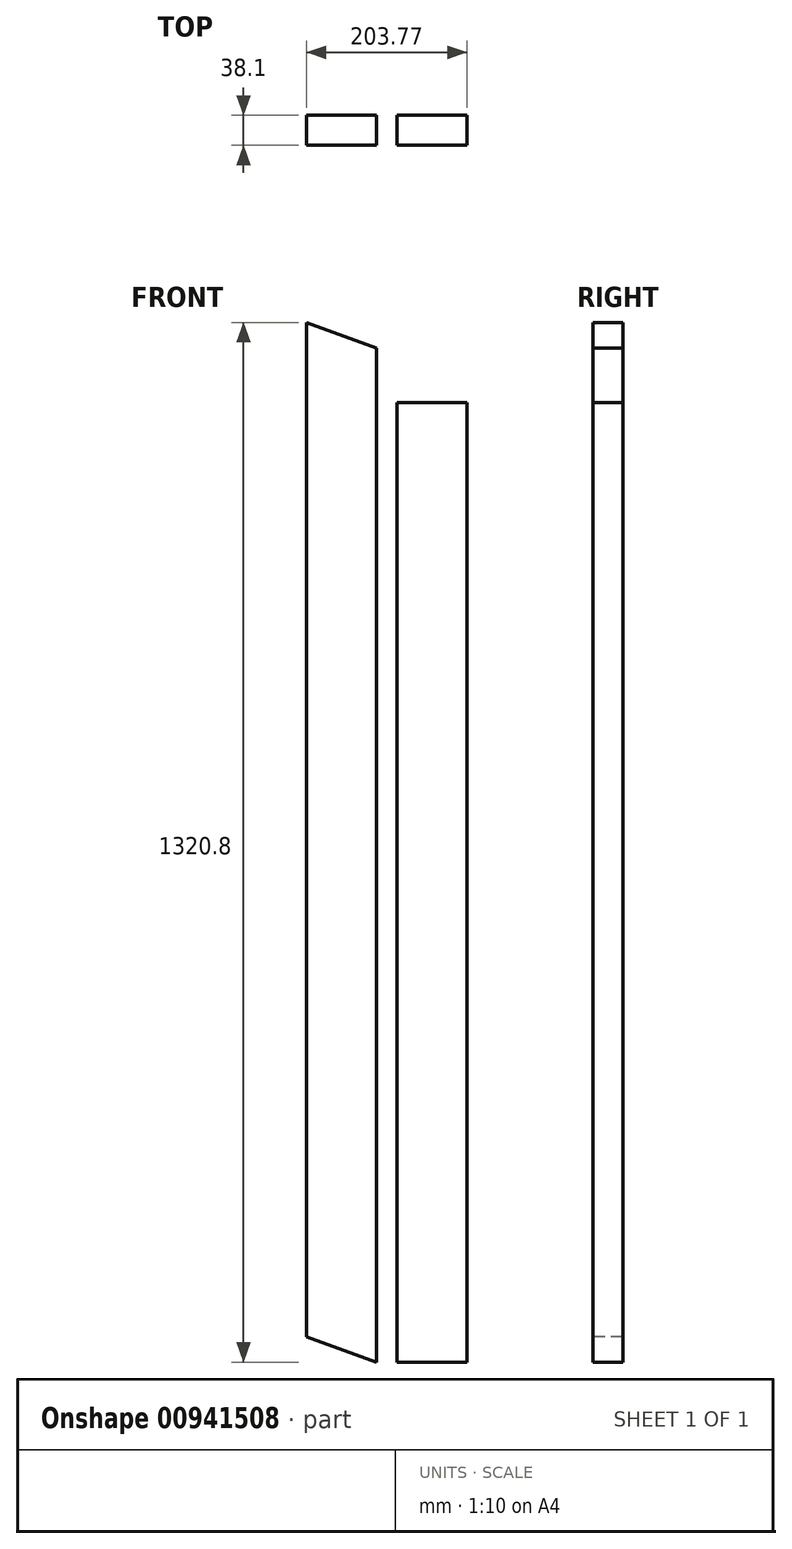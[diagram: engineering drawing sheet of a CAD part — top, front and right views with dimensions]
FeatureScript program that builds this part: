
annotation { "Feature Type Name" : "Feature", "Feature Type Description" : "" }
export const myFeature = defineFeature(function(context is Context, id is Id, definition is map)
    precondition{}
    {
        {
            var Q0;
            Q0=qCreatedBy(makeId("Front.planeOp"),FACE);
            var sketch = newSketch(context, id + "F0", { "sketchPlane" : qUnion([Q0])});
            skLineSegment(sketch, "E0.bottom", {"start": v(0, 0) * mm, "end": v(88.9, 0) * mm});
            skLineSegment(sketch, "E0.top", {"start": v(0, 1219.2) * mm, "end": v(88.9, 1219.2) * mm});
            skLineSegment(sketch, "E0.left", {"start": v(0, 0) * mm, "end": v(0, 1219.2) * mm});
            skLineSegment(sketch, "E0.right", {"start": v(88.9, 0) * mm, "end": v(88.9, 1219.2) * mm});
            skSolve(sketch);
        }
        {
            var Q0;
            Q0 = qSketchRegion(id + "F0", true);
            extrude(context, id + "F1", {"entities" : qUnion([Q0]), "depth" : 38.1 * mm, "offsetDistance" : 25.4 * mm});
        }
        {
            var Q0;
            Q0=qCreatedBy(makeId("Front.planeOp"),FACE);
            var sketch = newSketch(context, id + "F2", { "sketchPlane" : qUnion([Q0])});
            skLineSegment(sketch, "E1.bottom", {"start": v(-25.97, 0) * mm, "end": v(-114.87, 0) * mm});
            skLineSegment(sketch, "E1.top", {"start": v(-25.97, 1320.8) * mm, "end": v(-114.87, 1320.8) * mm});
            skLineSegment(sketch, "E1.left", {"start": v(-25.97, 0) * mm, "end": v(-25.97, 1320.8) * mm});
            skLineSegment(sketch, "E1.right", {"start": v(-114.87, 0) * mm, "end": v(-114.87, 1320.8) * mm});
            skSolve(sketch);
        }
        {
            var Q0;
            Q0 = qSketchRegion(id + "F2", true);
            extrude(context, id + "F3", {"entities" : qUnion([Q0]), "depth" : 38.1 * mm, "offsetDistance" : 25.4 * mm});
        }
        {
            var Q0;
            Q0=makeQuery(id+"F3.opExtrude","CAP_FACE",FACE,{"disambiguationData":[OSD([sQuery(id+"F2.wireOp",EDGE,"E1.bottom"),sQuery(id+"F2.wireOp",EDGE,"E1.top"),sQuery(id+"F2.wireOp",EDGE,"E1.left"),sQuery(id+"F2.wireOp",EDGE,"E1.right")])],"isStart":false});
            var sketch = newSketch(context, id + "F4", { "sketchPlane" : qUnion([Q0])});
            skLineSegment(sketch, "E2", {"start": v(-25.97, 0) * mm, "end": v(-114.87, 32.36) * mm});
            skLineSegment(sketch, "E3", {"start": v(-114.87, 32.36) * mm, "end": v(-114.87, 0) * mm});
            skLineSegment(sketch, "E4", {"start": v(-114.87, 0) * mm, "end": v(-25.97, 0) * mm});
            skLineSegment(sketch, "E5", {"start": v(-114.87, 1320.8) * mm, "end": v(-25.97, 1288.44) * mm});
            skLineSegment(sketch, "E6", {"start": v(-25.97, 1288.44) * mm, "end": v(-25.97, 1320.8) * mm});
            skLineSegment(sketch, "E7", {"start": v(-25.97, 1320.8) * mm, "end": v(-114.87, 1320.8) * mm});
            skSolve(sketch);
        }
        {
            var Q0;
            Q0 = qSketchRegion(id + "F4", true);
            extrude(context, id + "F5", {"entities" : qUnion([Q0]), "operationType" : NewBodyOperationType.REMOVE, "endBound" : BoundingType.THROUGH_ALL, "oppositeDirection" : true, "depth" : 25.4 * mm, "offsetDistance" : 25.4 * mm});
        }
    });
